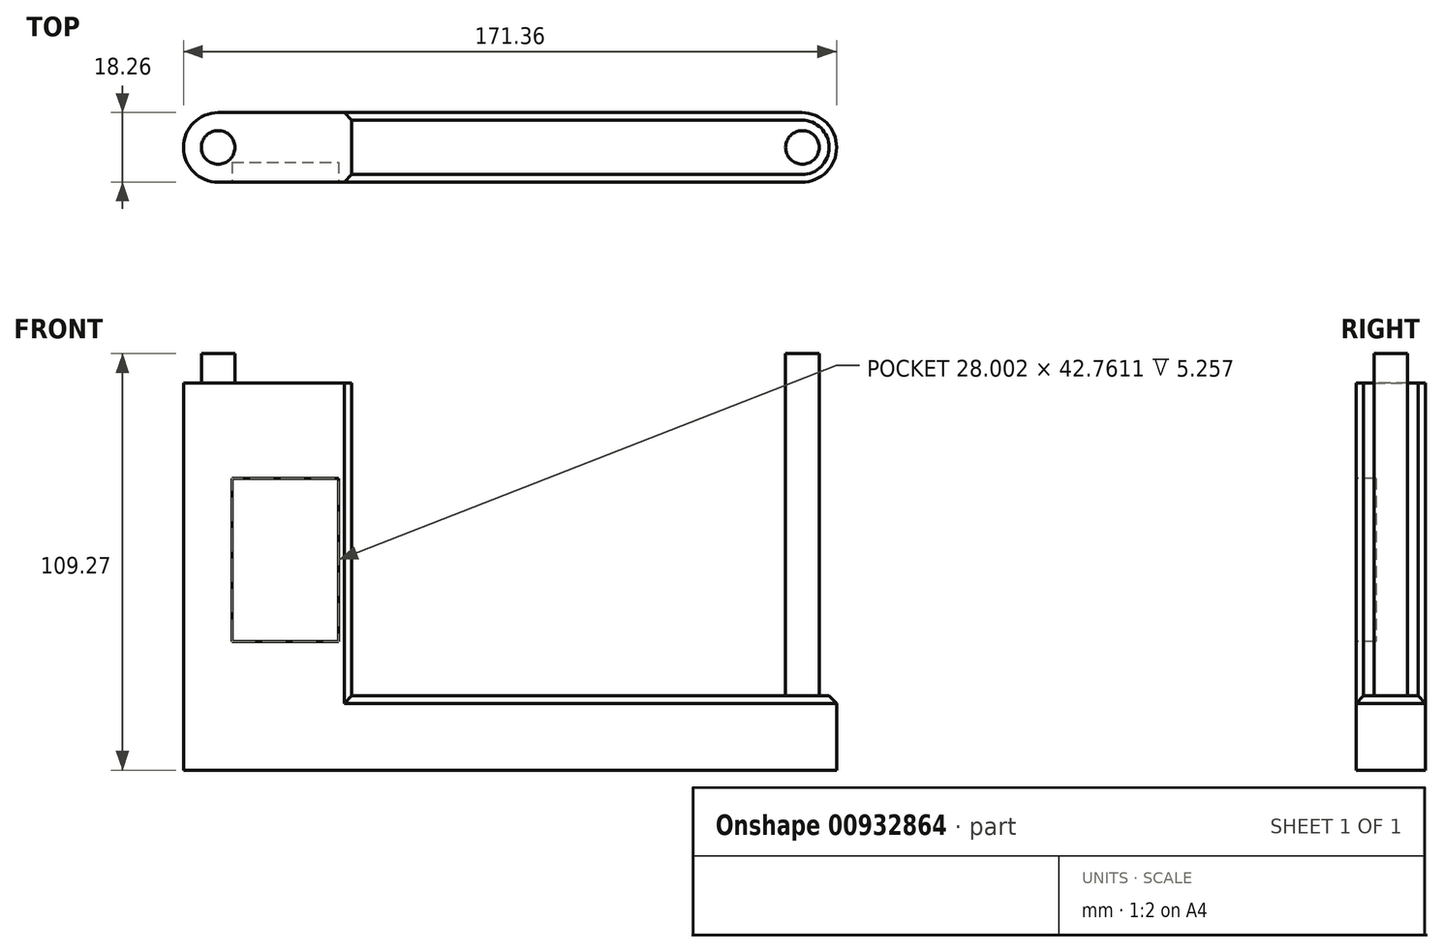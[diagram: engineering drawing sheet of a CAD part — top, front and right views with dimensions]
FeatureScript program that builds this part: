
annotation { "Feature Type Name" : "Feature", "Feature Type Description" : "" }
export const myFeature = defineFeature(function(context is Context, id is Id, definition is map)
    precondition{}
    {
        {
            var Q0;
            Q0=qCreatedBy(makeId("Top.planeOp"),FACE);
            var sketch = newSketch(context, id + "F0", { "sketchPlane" : qUnion([Q0])});
            skLineSegment(sketch, "E0.bottom", {"start": v(76.55, -9.13) * mm, "end": v(-76.55, -9.13) * mm});
            skLineSegment(sketch, "E0.top", {"start": v(76.55, 9.13) * mm, "end": v(-76.55, 9.13) * mm});
            skLineSegment(sketch, "E0.left", {"start": v(76.55, -9.13) * mm, "end": v(76.55, 9.13) * mm});
            skLineSegment(sketch, "E0.right", {"start": v(-76.55, -9.13) * mm, "end": v(-76.55, 9.13) * mm});
            skPoint(sketch, "E0.middle", {"position": v(0, 0) * mm});
            skArc(sketch, "E1", {"start": v(76.55, 9.13) * mm, "mid": v(85.68, 0) * mm, "end": v(76.55, -9.13) * mm});
            skArc(sketch, "E2", {"start": v(-76.55, -9.13) * mm, "mid": v(-85.68, 0) * mm, "end": v(-76.55, 9.13) * mm});
            skLineSegment(sketch, "E3", {"start": v(-41.5, 9.13) * mm, "end": v(-41.5, -9.13) * mm});
            skSolve(sketch);
        }
        {
            var Q0;
            Q0=makeQuery(id+"F0.imprint","IMPRINT",FACE,{"disambiguationData":[TD([[makeQuery(id+"F0.imprint","IMPRINT",EDGE,{"derivedFrom":sQuery(id+"F0.wireOp",EDGE,"E0.left")}),-1.0]])]});
            var Q1;
            {var subQ1=sQuery(id+"F0.wireOp",EDGE,"E0.left");Q1=makeQuery(id+"F0.imprint","IMPRINT",FACE,{"disambiguationData":[TD([[makeQuery(id+"F0.imprint","IMPRINT",EDGE,{"derivedFrom":subQ1}),1.0]])]});}
            extrude(context, id + "F1", {"entities" : qUnion([Q0, Q1]), "depth" : 19.48 * mm, "offsetDistance" : 25.4 * mm});
        }
        {
            var Q0;
            {var subQ1=sQuery(id+"F0.wireOp",EDGE,"E0.right");Q0=makeQuery(id+"F0.imprint","IMPRINT",FACE,{"disambiguationData":[TD([[makeQuery(id+"F0.imprint","IMPRINT",EDGE,{"derivedFrom":subQ1}),-1.0]])]});}
            var Q1;
            Q1=makeQuery(id+"F0.imprint","IMPRINT",FACE,{"disambiguationData":[TD([[makeQuery(id+"F0.imprint","IMPRINT",EDGE,{"derivedFrom":sQuery(id+"F0.wireOp",EDGE,"E0.right")}),1.0]])]});
            extrude(context, id + "F2", {"entities" : qUnion([Q0, Q1]), "operationType" : NewBodyOperationType.ADD, "depth" : 101.6 * mm, "offsetDistance" : 25.4 * mm});
        }
        {
            var Q0;
            {var subQ0=sQuery(id+"F0.wireOp",EDGE,"E0.bottom");Q0=makeQuery(id+"F2.boolean.opBoolean","MERGE",FACE,{"derivedFrom":[makeQuery(id+"F1.opExtrude","SWEPT_FACE",FACE,{"disambiguationData":[OSD([subQ0])]}),makeQuery(id+"F2.opExtrude","SWEPT_FACE",FACE,{"disambiguationData":[OSD([subQ0])]})]});}
            var sketch = newSketch(context, id + "F3", { "sketchPlane" : qUnion([Q0])});
            skLineSegment(sketch, "E4.bottom", {"start": v(-72.94, 76.57) * mm, "end": v(-44.94, 76.57) * mm});
            skLineSegment(sketch, "E4.top", {"start": v(-72.94, 33.8) * mm, "end": v(-44.94, 33.8) * mm});
            skLineSegment(sketch, "E4.left", {"start": v(-72.94, 76.57) * mm, "end": v(-72.94, 33.8) * mm});
            skLineSegment(sketch, "E4.right", {"start": v(-44.94, 76.57) * mm, "end": v(-44.94, 33.8) * mm});
            skSolve(sketch);
        }
        {
            var Q0;
            Q0=makeQuery(id+"F3.imprint","IMPRINT",FACE,{"disambiguationData":[TD([[makeQuery(id+"F3.imprint","IMPRINT",EDGE,{"derivedFrom":sQuery(id+"F3.wireOp",EDGE,"E4.bottom")}),-1.0]])]});
            extrude(context, id + "F4", {"entities" : qUnion([Q0]), "operationType" : NewBodyOperationType.REMOVE, "oppositeDirection" : true, "depth" : 5.26 * mm, "offsetDistance" : 25.4 * mm});
        }
        {
            var Q0;
            Q0=makeQuery(id+"F2.opExtrude","CAP_FACE",FACE,{"disambiguationData":[OSD([sQuery(id+"F0.wireOp",EDGE,"E0.bottom"),sQuery(id+"F0.wireOp",EDGE,"E0.top"),sQuery(id+"F0.wireOp",EDGE,"E2"),sQuery(id+"F0.wireOp",EDGE,"E3")])],"isStart":false});
            var sketch = newSketch(context, id + "F5", { "sketchPlane" : qUnion([Q0])});
            skLineSegment(sketch, "E5.bottom", {"start": v(105.6, -51.77) * mm, "end": v(-105.6, -51.77) * mm});
            skLineSegment(sketch, "E5.top", {"start": v(105.6, 51.77) * mm, "end": v(-105.6, 51.77) * mm});
            skLineSegment(sketch, "E5.left", {"start": v(105.6, -51.77) * mm, "end": v(105.6, 51.77) * mm});
            skLineSegment(sketch, "E5.right", {"start": v(-105.6, -51.77) * mm, "end": v(-105.6, 51.77) * mm});
            skPoint(sketch, "E5.middle", {"position": v(0, 0) * mm});
            skSolve(sketch);
        }
        {
            var Q0;
            Q0=makeQuery(id+"F5.imprint","IMPRINT",FACE,{"disambiguationData":[TD([[makeQuery(id+"F5.imprint","IMPRINT",EDGE,{"derivedFrom":sQuery(id+"F5.wireOp",EDGE,"E5.bottom")}),-1.0]])]});
            var Q1;
            Q1=sQuery(id+"F5.wireOp",EDGE,"E5.bottom");
            var Q2;
            Q2=sQuery(id+"F5.wireOp",EDGE,"E5.right");
            var Q3;
            Q3=sQuery(id+"F5.wireOp",EDGE,"E5.top");
            var Q4;
            Q4=sQuery(id+"F5.wireOp",EDGE,"E5.left");
            extrude(context, id + "F6", {"entities" : qUnion([Q0]), "bodyType" : ToolBodyType.SURFACE, "surfaceEntities" : qUnion([Q1, Q2, Q3, Q4]), "depth" : 10 * mm, "offsetDistance" : 25.4 * mm});
        }
        {
            var Q0;
            Q0=makeQuery(id+"F6.opExtrude","SWEPT_EDGE",EDGE,{"disambiguationData":[OSD([sQuery(id+"F5.wireOp",VERTEX,"E5.right.start")])]});
            var Q1;
            Q1=makeQuery(id+"F6.opExtrude","SWEPT_EDGE",EDGE,{"disambiguationData":[OSD([sQuery(id+"F5.wireOp",VERTEX,"E5.top.end")])]});
            var Q2;
            Q2=makeQuery(id+"F6.opExtrude","SWEPT_EDGE",EDGE,{"disambiguationData":[OSD([sQuery(id+"F5.wireOp",VERTEX,"E5.left.end")])]});
            var Q3;
            Q3=makeQuery(id+"F6.opExtrude","SWEPT_EDGE",EDGE,{"disambiguationData":[OSD([sQuery(id+"F5.wireOp",VERTEX,"E5.left.start")])]});
            fillet(context, id + "F7", {"entities" : qUnion([Q0, Q1, Q2, Q3]), "radius" : 5.08 * mm, "tangentPropagation" : true, "allowEdgeOverflow" : false});
        }
        {
            var Q0;
            Q0=qCreatedBy(makeId("Top.planeOp"),FACE);
            var sketch = newSketch(context, id + "F8", { "sketchPlane" : qUnion([Q0])});
            skCircle(sketch, "E6", {"center": v(76.7, 0) * mm, "radius": 4.4 * mm});
            skCircle(sketch, "E7", {"center": v(-76.57, 0) * mm, "radius": 4.4 * mm});
            skSolve(sketch);
        }
        {
            var Q0;
            Q0=makeQuery(id+"F8.imprint","IMPRINT",FACE,{"disambiguationData":[TD([[makeQuery(id+"F8.imprint","IMPRINT",EDGE,{"derivedFrom":sQuery(id+"F8.wireOp",EDGE,"E6")}),1.0]])]});
            var Q1;
            Q1=makeQuery(id+"F8.imprint","IMPRINT",FACE,{"disambiguationData":[TD([[makeQuery(id+"F8.imprint","IMPRINT",EDGE,{"derivedFrom":sQuery(id+"F8.wireOp",EDGE,"E7")}),1.0]])]});
            extrude(context, id + "F9", {"entities" : qUnion([Q0, Q1]), "operationType" : NewBodyOperationType.ADD, "depth" : 109.27 * mm, "offsetDistance" : 25.4 * mm});
        }
        {
            var Q0;
            Q0=makeQuery(id+"F2.opExtrude","SWEPT_EDGE",EDGE,{"disambiguationData":[OSD([sQuery(id+"F0.wireOp",EDGE,"E0.bottom"),sQuery(id+"F0.wireOp",EDGE,"E3")])]});
            var Q1;
            Q1=makeQuery(id+"F1.opExtrude","CAP_EDGE",EDGE,{"disambiguationData":[OSD([sQuery(id+"F0.wireOp",EDGE,"E0.bottom")])],"isStart":false});
            var Q2;
            Q2=makeQuery(id+"F2.opExtrude","SWEPT_EDGE",EDGE,{"disambiguationData":[OSD([sQuery(id+"F0.wireOp",EDGE,"E0.top"),sQuery(id+"F0.wireOp",EDGE,"E3")])]});
            chamfer(context, id + "F10", {"entities" : qUnion([Q0, Q1, Q2]), "width" : 2 * mm, "tangentPropagation" : true});
        }
    });
